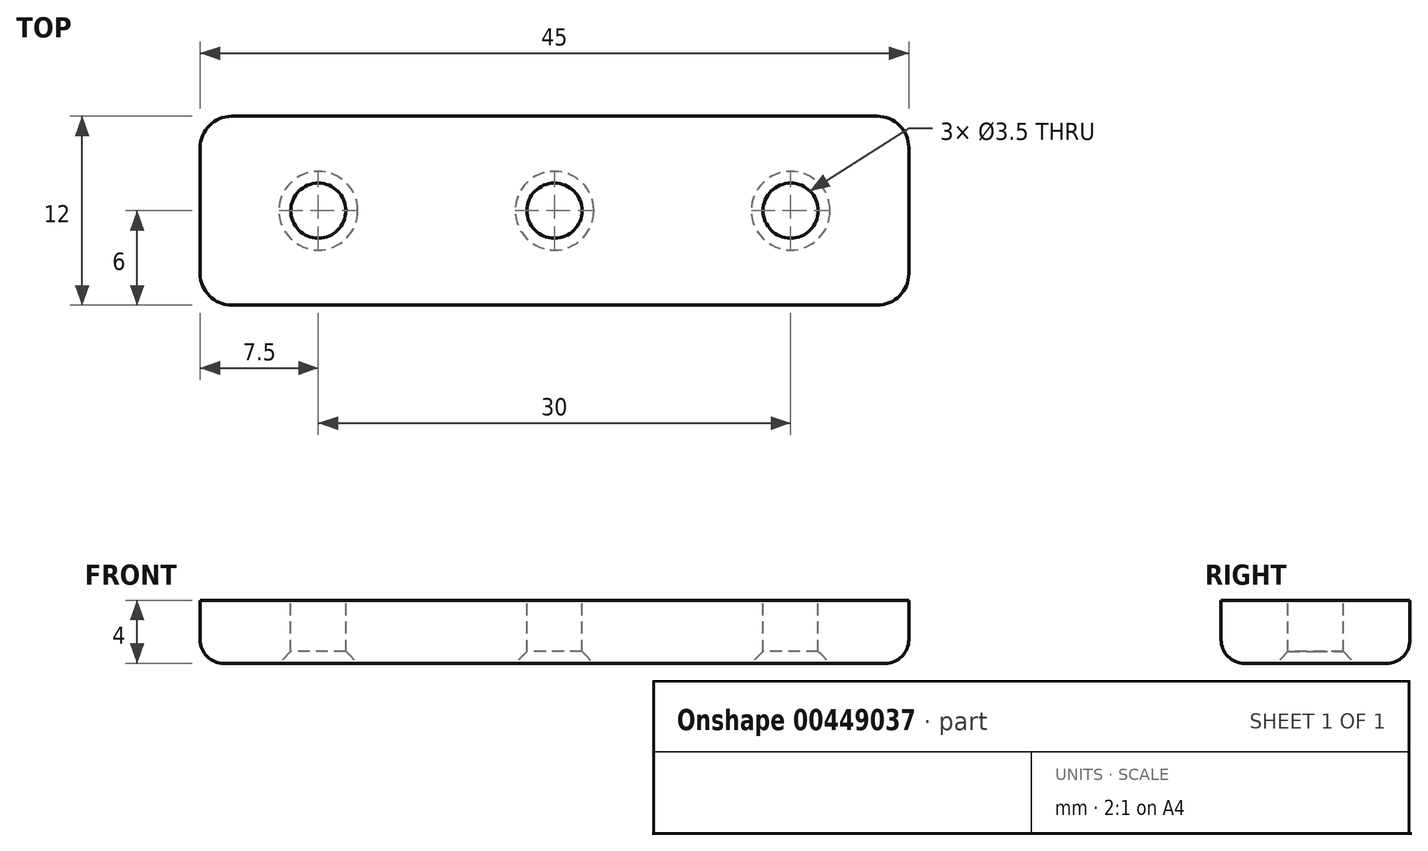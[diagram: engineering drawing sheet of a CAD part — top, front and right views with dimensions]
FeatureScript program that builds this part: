
annotation { "Feature Type Name" : "Feature", "Feature Type Description" : "" }
export const myFeature = defineFeature(function(context is Context, id is Id, definition is map)
    precondition{}
    {
        {
            var Q0;
            Q0=qCreatedBy(makeId("Top.planeOp"),FACE);
            var sketch = newSketch(context, id + "F0", { "sketchPlane" : qUnion([Q0])});
            skLineSegment(sketch, "E0.bottom", {"start": v(-22.5, 6) * mm, "end": v(22.5, 6) * mm});
            skLineSegment(sketch, "E0.top", {"start": v(-22.5, -6) * mm, "end": v(22.5, -6) * mm});
            skLineSegment(sketch, "E0.left", {"start": v(-22.5, 6) * mm, "end": v(-22.5, -6) * mm});
            skLineSegment(sketch, "E0.right", {"start": v(22.5, 6) * mm, "end": v(22.5, -6) * mm});
            skPoint(sketch, "E0.middle", {"position": v(0, 0) * mm});
            skPoint(sketch, "E1", {"position": v(15, 0) * mm});
            skPoint(sketch, "E2", {"position": v(-15, 0) * mm});
            skSolve(sketch);
        }
        {
            var Q0;
            Q0=makeQuery(id+"F0.imprint","IMPRINT",FACE,{"disambiguationData":[TD([[makeQuery(id+"F0.imprint","IMPRINT",EDGE,{"derivedFrom":sQuery(id+"F0.wireOp",EDGE,"E0.bottom")}),-1.0]])]});
            extrude(context, id + "F1", {"entities" : qUnion([Q0]), "depth" : 4 * mm});
        }
        {
            var Q0;
            Q0=sQuery(id+"F0.wireOp",VERTEX,"E2");
            var Q1;
            Q1=sQuery(id+"F0.wireOp",VERTEX,"E0.middle");
            var Q2;
            Q2=sQuery(id+"F0.wireOp",VERTEX,"E1");
            var Q3;
            Q3=makeQuery(id+"F1.opExtrude","SWEPT_BODY",BODY,{"disambiguationData":[OSD([sQuery(id+"F0.wireOp",EDGE,"E0.bottom"),sQuery(id+"F0.wireOp",EDGE,"E0.top"),sQuery(id+"F0.wireOp",EDGE,"E0.left"),sQuery(id+"F0.wireOp",EDGE,"E0.right")])]});
            hole(context, id + "F2", {"style" : HoleStyle.C_SINK, "endStyle" : HoleEndStyle.THROUGH, "oppositeDirection" : true, "holeDiameter" : 3.5 * mm, "cSinkDiameter" : 5 * mm, "cSinkAngle" : 90 * degree, "isTappedThrough" : true, "tappedDepth" : 12 * mm, "tapClearance" : 3, "startFromSketch" : true, "locations" : qUnion([Q0, Q1, Q2]), "scope" : qUnion([Q3])});
        }
        {
            var Q0;
            Q0=makeQuery(id+"F1.opExtrude","CAP_EDGE",EDGE,{"disambiguationData":[OSD([sQuery(id+"F0.wireOp",EDGE,"E0.top")])],"isStart":true});
            var Q1;
            Q1=makeQuery(id+"F1.opExtrude","CAP_EDGE",EDGE,{"disambiguationData":[OSD([sQuery(id+"F0.wireOp",EDGE,"E0.left")])],"isStart":true});
            var Q2;
            Q2=makeQuery(id+"F1.opExtrude","CAP_EDGE",EDGE,{"disambiguationData":[OSD([sQuery(id+"F0.wireOp",EDGE,"E0.bottom")])],"isStart":true});
            var Q3;
            Q3=makeQuery(id+"F1.opExtrude","CAP_EDGE",EDGE,{"disambiguationData":[OSD([sQuery(id+"F0.wireOp",EDGE,"E0.right")])],"isStart":true});
            fillet(context, id + "F3", {"entities" : qUnion([Q0, Q1, Q2, Q3]), "radius" : 1.5 * mm, "tangentPropagation" : true, "allowEdgeOverflow" : false});
        }
        {
            var Q0;
            Q0=makeQuery(id+"F3.opFillet","BLEND_EDGE",EDGE,{"blendedFrom":[makeQuery(id+"F1.opExtrude","CAP_EDGE",EDGE,{"disambiguationData":[OSD([sQuery(id+"F0.wireOp",EDGE,"E0.bottom")])],"isStart":true}),makeQuery(id+"F1.opExtrude","CAP_EDGE",EDGE,{"disambiguationData":[OSD([sQuery(id+"F0.wireOp",EDGE,"E0.left")])],"isStart":true})],"blendedInto":[]});
            var Q1;
            Q1=makeQuery(id+"F3.opFillet","BLEND_EDGE",EDGE,{"blendedFrom":[makeQuery(id+"F1.opExtrude","CAP_EDGE",EDGE,{"disambiguationData":[OSD([sQuery(id+"F0.wireOp",EDGE,"E0.top")])],"isStart":true}),makeQuery(id+"F1.opExtrude","CAP_EDGE",EDGE,{"disambiguationData":[OSD([sQuery(id+"F0.wireOp",EDGE,"E0.left")])],"isStart":true})],"blendedInto":[]});
            var Q2;
            Q2=makeQuery(id+"F3.opFillet","BLEND_EDGE",EDGE,{"blendedFrom":[makeQuery(id+"F1.opExtrude","CAP_EDGE",EDGE,{"disambiguationData":[OSD([sQuery(id+"F0.wireOp",EDGE,"E0.bottom")])],"isStart":true}),makeQuery(id+"F1.opExtrude","CAP_EDGE",EDGE,{"disambiguationData":[OSD([sQuery(id+"F0.wireOp",EDGE,"E0.right")])],"isStart":true})],"blendedInto":[]});
            var Q3;
            Q3=makeQuery(id+"F3.opFillet","BLEND_EDGE",EDGE,{"blendedFrom":[makeQuery(id+"F1.opExtrude","CAP_EDGE",EDGE,{"disambiguationData":[OSD([sQuery(id+"F0.wireOp",EDGE,"E0.top")])],"isStart":true}),makeQuery(id+"F1.opExtrude","CAP_EDGE",EDGE,{"disambiguationData":[OSD([sQuery(id+"F0.wireOp",EDGE,"E0.right")])],"isStart":true})],"blendedInto":[]});
            fillet(context, id + "F4", {"entities" : qUnion([Q0, Q1, Q2, Q3]), "radius" : 2 * mm, "tangentPropagation" : true, "allowEdgeOverflow" : false});
        }
    });
